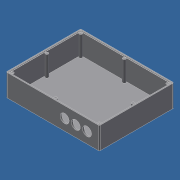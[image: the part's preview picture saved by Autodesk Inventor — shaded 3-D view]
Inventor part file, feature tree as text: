
AUTODESK INVENTOR PART (.ipt)
format: ipt  version: 2015 SP2 (Build 190223200, 223)  size: 223,744 bytes
history: native  units: mm (DEFAULTED — no unit token found)
features: other x8, sketch x8, extrude x7, fillet x1, hole x1
bodies: Solide1 (feature_tree)
feature tree (25):
  other  "Origine"
  extrude  "Extrusion1"  Depth=250.0mm
  extrude  "Extrusion2"  Depth=200.0mm
  extrude  "Extrusion3"  Depth=59.0mm TaperAngle=0.0deg
  fillet  "Congé1"  Radius=4.3mm
  extrude  "Extrusion4"  Depth=4.3mm
  extrude  "Extrusion5"  Depth=57.0mm TaperAngle=0.0deg
  hole  "Perçage1"  [1 undecoded]
  extrude  "Extrusion6"  Depth=3.3mm
  extrude  "Extrusion7"  Depth=2.0mm TaperAngle=0.0deg
  other  "Plan YZ"
  other  "Plan XZ"
  other  "Plan XY"
  other  "Axe X"
  other  "Axe Y"
  other  "Axe Z"
  other  "Point de centre"
  sketch  "Esquisse1"
  sketch  "Esquisse6"
  sketch  "Esquisse7"
  sketch  "Esquisse9"
  sketch  "Esquisse10"
  sketch  "Esquisse12"
  sketch  "Esquisse13"
  sketch  "Esquisse14"
note: 1 required parameter value undecoded (feature->parameter linkage not recoverable at this tier; creation-order binding heuristic only, values carry confidence <= 0.55)
